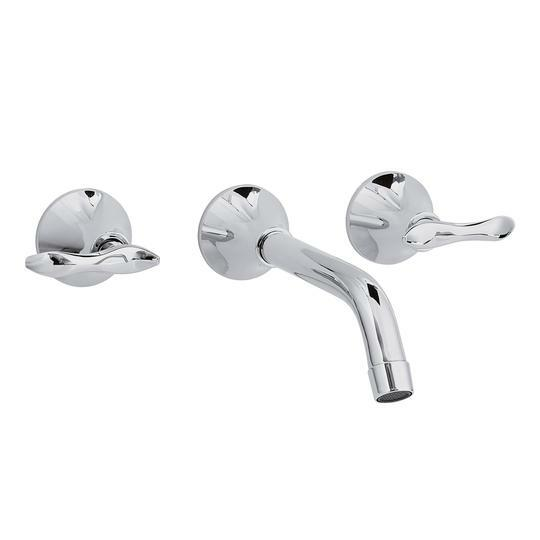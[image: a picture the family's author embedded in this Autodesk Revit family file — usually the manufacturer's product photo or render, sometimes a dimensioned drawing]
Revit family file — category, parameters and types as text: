
# Revit family: GS-1816-11 MEZCLADOR LAVAMANOS PARED TEDESCA
name_source: partatom
category: Plumbing Fixtures
revit_build: Autodesk Revit 2018 (Build: 20170223_1515(x64)
units: mm (PartAtom-declared; Revit-internal decimal feet)

## family parameters
Cut with Voids When Loaded = No
Host = Face
OmniClass Number = 23.31.11.00
Part Type = Normal
Room Calculation Point = No
Round Connector Dimension = Use Diameter
Shared = No

## types (1)
- SG-1816-11
    Base - Aireador = 215 mm
    CW Connection = Yes
    Default Elevation = 0 mm  [stored 0 ft]
    Description = Mezclador Lavamanos
    Dim escudo = 60 mm  [stored 0.19685 ft]
    Distancia entre griferias = 203 mm
    HW Connection = Yes
    Link Ficha Tecnica = https://infotecnica.gricol.com
    Manija = 80 mm  [stored 0.262467 ft]
    Manufacturer = Gricol
    Metal Laton Cromado = Metal Laton Cromado
    Mezclador = Mezclador
    Model = GS-1816-11
    Plastico - ABS Cromado = Plastico - ABS Cromado
    Product Name = MEZCLADOR LAVAMANOS PARED TEDESCA
    Type Image = <None>
    URL = https://www.gricol.com
    Vent Connection = No
    Waste Connection = No

note: [stored X ft] marks values corroborated as IEEE doubles in the binary element streams (Revit-internal decimal feet)

## geometry (parser evidence)
native form markers: Blend x2, Sweep x9
no freeform markers — native parametric forms only
